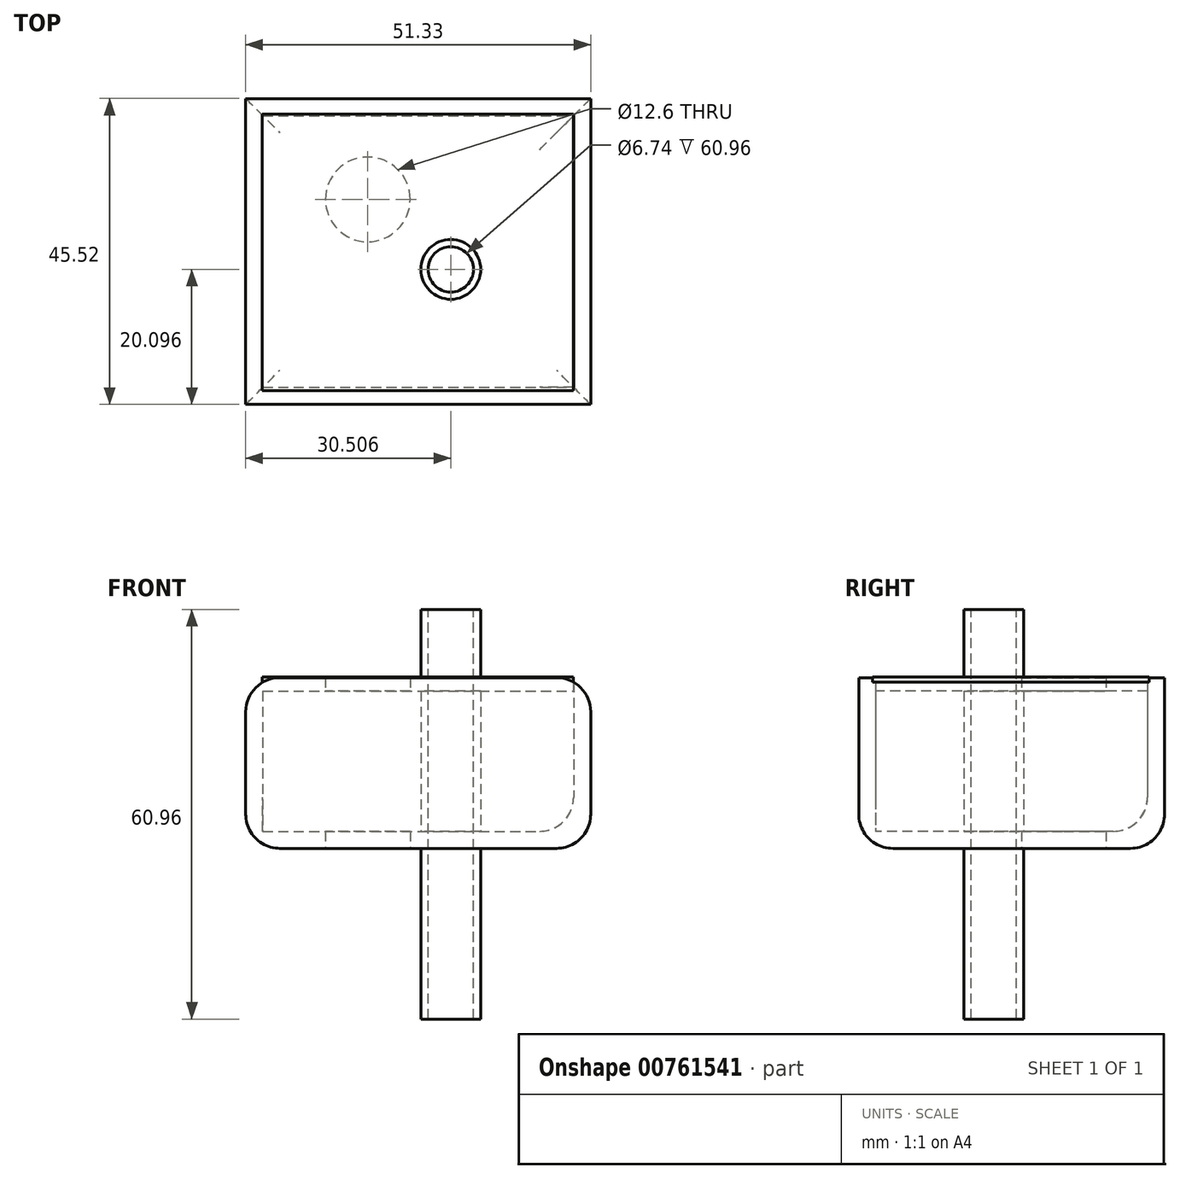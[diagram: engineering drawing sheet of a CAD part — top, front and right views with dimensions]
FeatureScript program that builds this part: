
annotation { "Feature Type Name" : "Feature", "Feature Type Description" : "" }
export const myFeature = defineFeature(function(context is Context, id is Id, definition is map)
    precondition{}
    {
        {
            var Q0;
            Q0=qCreatedBy(makeId("Top.planeOp"),FACE);
            var sketch = newSketch(context, id + "F0", { "sketchPlane" : qUnion([Q0])});
            skLineSegment(sketch, "E0.bottom", {"start": v(-26.39, 20.34) * mm, "end": v(24.94, 20.34) * mm});
            skLineSegment(sketch, "E0.top", {"start": v(-26.39, -25.18) * mm, "end": v(24.94, -25.18) * mm});
            skLineSegment(sketch, "E0.left", {"start": v(-26.39, 20.34) * mm, "end": v(-26.39, -25.18) * mm});
            skLineSegment(sketch, "E0.right", {"start": v(24.94, 20.34) * mm, "end": v(24.94, -25.18) * mm});
            skSolve(sketch);
        }
        {
            var Q0;
            Q0 = qSketchRegion(id + "F0", true);
            extrude(context, id + "F1", {"entities" : qUnion([Q0]), "depth" : 25.4 * mm, "offsetDistance" : 25.4 * mm});
        }
        {
            var Q0;
            Q0=makeQuery(id+"F1.opExtrude","CAP_FACE",FACE,{"disambiguationData":[OSD([sQuery(id+"F0.wireOp",EDGE,"E0.bottom"),sQuery(id+"F0.wireOp",EDGE,"E0.top"),sQuery(id+"F0.wireOp",EDGE,"E0.left"),sQuery(id+"F0.wireOp",EDGE,"E0.right")])],"isStart":false});
            shell(context, id + "F2", {"entities" : qUnion([Q0]), "thickness" : 2.54 * mm});
        }
        {
            var Q0;
            Q0=makeQuery(id+"F1.opExtrude","CAP_EDGE",EDGE,{"disambiguationData":[OSD([sQuery(id+"F0.wireOp",EDGE,"E0.top")])],"isStart":true});
            var Q1;
            Q1=makeQuery(id+"F1.opExtrude","CAP_EDGE",EDGE,{"disambiguationData":[OSD([sQuery(id+"F0.wireOp",EDGE,"E0.left")])],"isStart":true});
            var Q2;
            {var subQ0=sQuery(id+"F0.wireOp",EDGE,"E0.bottom");Q2=makeQuery(id+"F2.opShell","OFFSET_EDGE",EDGE,{"disambiguationData":[OSD([subQ0]),TDD([makeQuery(id+"F1.opExtrude","CAP_EDGE",EDGE,{"disambiguationData":[OSD([subQ0])],"isStart":true})])]});}
            var Q3;
            {var subQ0=sQuery(id+"F0.wireOp",EDGE,"E0.right");Q3=makeQuery(id+"F2.opShell","OFFSET_EDGE",EDGE,{"disambiguationData":[OSD([subQ0]),TDD([makeQuery(id+"F1.opExtrude","CAP_EDGE",EDGE,{"disambiguationData":[OSD([subQ0])],"isStart":true})])]});}
            var Q4;
            Q4=makeQuery(id+"F1.opExtrude","CAP_EDGE",EDGE,{"disambiguationData":[OSD([sQuery(id+"F0.wireOp",EDGE,"E0.bottom")])],"isStart":true});
            var Q5;
            Q5=makeQuery(id+"F1.opExtrude","CAP_EDGE",EDGE,{"disambiguationData":[OSD([sQuery(id+"F0.wireOp",EDGE,"E0.right")])],"isStart":true});
            fillet(context, id + "F3", {"entities" : qUnion([Q0, Q1, Q2, Q3, Q4, Q5]), "radius" : 5.08 * mm, "tangentPropagation" : true, "allowEdgeOverflow" : false});
        }
        {
            var Q0;
            Q0=qCreatedBy(makeId("Front.planeOp"),FACE);
            var sketch = newSketch(context, id + "F4", { "sketchPlane" : qUnion([Q0])});
            skLineSegment(sketch, "E1.bottom", {"start": v(-23.91, 25.53) * mm, "end": v(22.38, 25.53) * mm});
            skLineSegment(sketch, "E1.top", {"start": v(-23.91, 23.39) * mm, "end": v(22.38, 23.39) * mm});
            skLineSegment(sketch, "E1.left", {"start": v(-23.91, 25.53) * mm, "end": v(-23.91, 23.39) * mm});
            skLineSegment(sketch, "E1.right", {"start": v(22.38, 25.53) * mm, "end": v(22.38, 23.39) * mm});
            skSolve(sketch);
        }
        {
            var Q0;
            Q0 = qSketchRegion(id + "F4", true);
            extrude(context, id + "F5", {"entities" : qUnion([Q0]), "operationType" : NewBodyOperationType.ADD, "depth" : 23.1 * mm, "offsetDistance" : 25.4 * mm, "hasSecondDirection" : true, "secondDirectionOppositeDirection" : true, "secondDirectionDepth" : 18.03 * mm});
        }
        {
            var Q0;
            Q0=qCreatedBy(makeId("Top.planeOp"),FACE);
            var sketch = newSketch(context, id + "F6", { "sketchPlane" : qUnion([Q0])});
            skCircle(sketch, "E2", {"center": v(-8.23, 5.33) * mm, "radius": 6.3 * mm});
            skSolve(sketch);
        }
        {
            var Q0;
            Q0 = qSketchRegion(id + "F6", true);
            extrude(context, id + "F7", {"entities" : qUnion([Q0]), "operationType" : NewBodyOperationType.REMOVE, "depth" : 25.4 * mm, "offsetDistance" : 25.4 * mm, "hasSecondDirection" : true, "secondDirectionOppositeDirection" : true, "secondDirectionDepth" : 36.83 * mm});
        }
        {
            var Q0;
            Q0=qCreatedBy(makeId("Top.planeOp"),FACE);
            var sketch = newSketch(context, id + "F8", { "sketchPlane" : qUnion([Q0])});
            skCircle(sketch, "E3", {"center": v(4.12, -5.08) * mm, "radius": 4.45 * mm});
            skSolve(sketch);
        }
        {
            var Q0;
            Q0 = qSketchRegion(id + "F8", true);
            extrude(context, id + "F9", {"entities" : qUnion([Q0]), "operationType" : NewBodyOperationType.ADD, "depth" : 35.56 * mm, "offsetDistance" : 25.4 * mm, "hasSecondDirection" : true, "secondDirectionOppositeDirection" : true, "secondDirectionDepth" : 25.4 * mm});
        }
        {
            var Q0;
            Q0=qCreatedBy(makeId("Top.planeOp"),FACE);
            var sketch = newSketch(context, id + "F10", { "sketchPlane" : qUnion([Q0])});
            skCircle(sketch, "E4", {"center": v(4.12, -5.08) * mm, "radius": 3.37 * mm});
            skSolve(sketch);
        }
        {
            var Q0;
            Q0 = qSketchRegion(id + "F10", true);
            extrude(context, id + "F11", {"entities" : qUnion([Q0]), "operationType" : NewBodyOperationType.REMOVE, "oppositeDirection" : true, "depth" : 27.7 * mm, "offsetDistance" : 25.4 * mm, "hasSecondDirection" : true, "secondDirectionOppositeDirection" : false, "secondDirectionDepth" : 52.22 * mm});
        }
        {
            var Q0;
            Q0=makeQuery(id+"F1.opExtrude","CAP_EDGE",EDGE,{"disambiguationData":[OSD([sQuery(id+"F0.wireOp",EDGE,"E0.right")])],"isStart":false});
            var Q1;
            Q1=makeQuery(id+"F1.opExtrude","CAP_EDGE",EDGE,{"disambiguationData":[OSD([sQuery(id+"F0.wireOp",EDGE,"E0.left")])],"isStart":false});
            fillet(context, id + "F12", {"entities" : qUnion([Q0, Q1]), "radius" : 5.08 * mm, "tangentPropagation" : true, "allowEdgeOverflow" : false});
        }
    });
